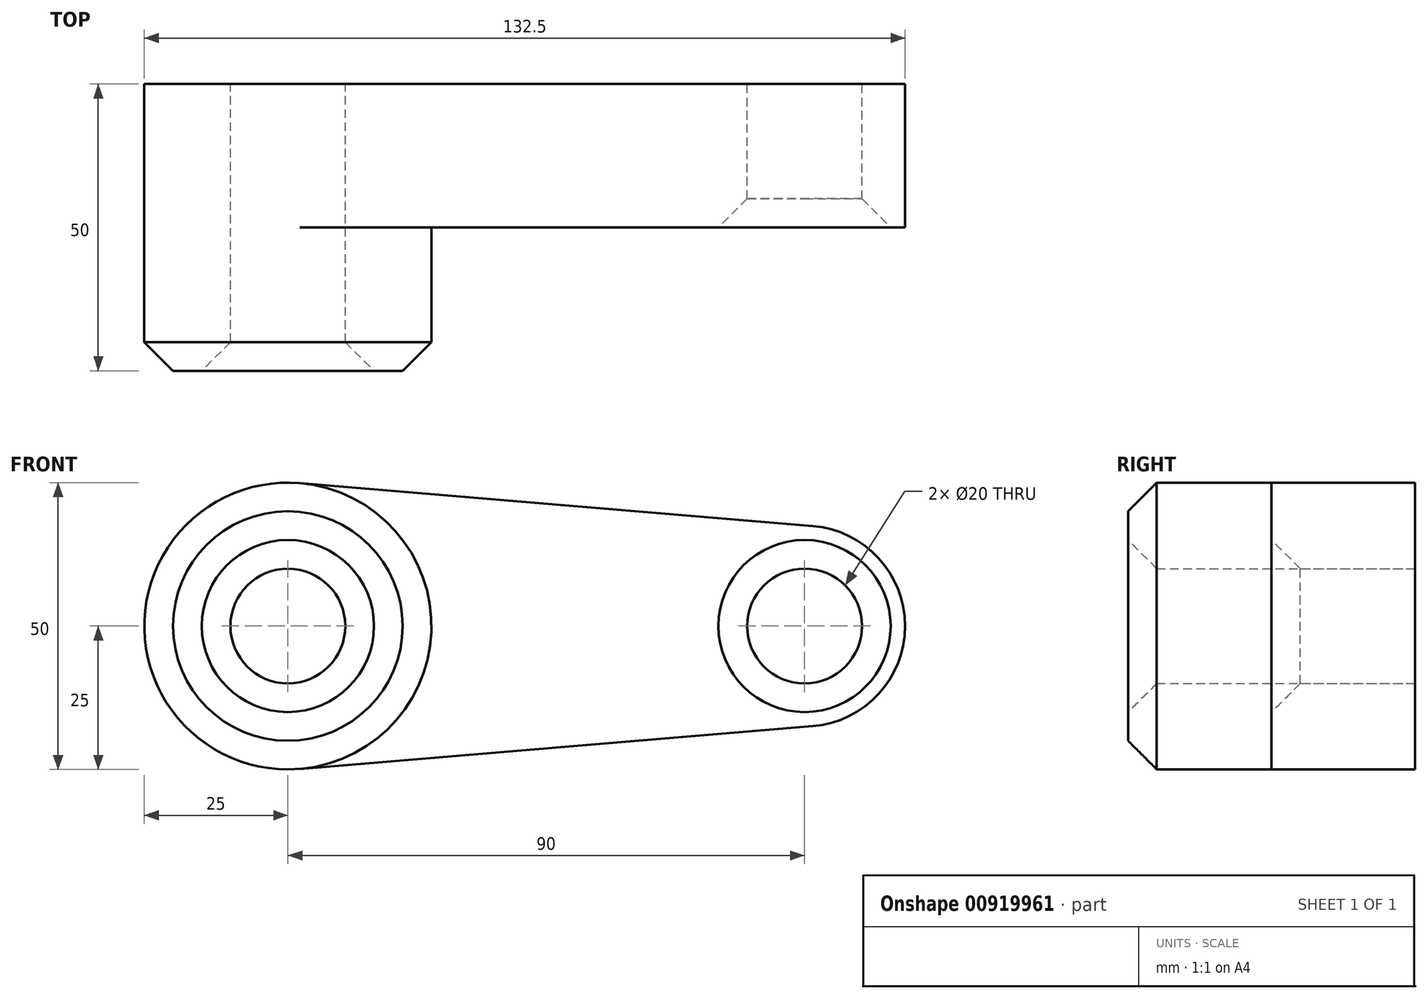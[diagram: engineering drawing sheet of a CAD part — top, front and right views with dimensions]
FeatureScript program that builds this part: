
annotation { "Feature Type Name" : "Feature", "Feature Type Description" : "" }
export const myFeature = defineFeature(function(context is Context, id is Id, definition is map)
    precondition{}
    {
        {
            var Q0;
            Q0=qCreatedBy(makeId("Front.planeOp"),FACE);
            var sketch = newSketch(context, id + "F0", { "sketchPlane" : qUnion([Q0])});
            skCircle(sketch, "E0", {"center": v(0, 0) * mm, "radius": 25 * mm});
            skCircle(sketch, "E1", {"center": v(90, 0) * mm, "radius": 17.5 * mm});
            skLineSegment(sketch, "E2", {"start": v(2.08, 24.91) * mm, "end": v(91.46, 17.44) * mm});
            skLineSegment(sketch, "E3", {"start": v(2.08, -24.91) * mm, "end": v(91.46, -17.44) * mm});
            skCircle(sketch, "E4", {"center": v(0, 0) * mm, "radius": 10 * mm});
            skCircle(sketch, "E5", {"center": v(90, 0) * mm, "radius": 10 * mm});
            skSolve(sketch);
        }
        {
            var Q0;
            {var subQ0=sQuery(id+"F0.wireOp",EDGE,"E2");Q0=makeQuery(id+"F0.imprint","IMPRINT",FACE,{"disambiguationData":[TD([[makeQuery(id+"F0.imprint","IMPRINT",EDGE,{"derivedFrom":subQ0}),-1.0]])]});}
            var Q1;
            Q1=makeQuery(id+"F0.imprint","IMPRINT",FACE,{"disambiguationData":[TD([[makeQuery(id+"F0.imprint","IMPRINT",EDGE,{"derivedFrom":sQuery(id+"F0.wireOp",EDGE,"E5")}),-1.0]])]});
            var Q2;
            Q2=makeQuery(id+"F0.imprint","IMPRINT",FACE,{"disambiguationData":[TD([[makeQuery(id+"F0.imprint","IMPRINT",EDGE,{"derivedFrom":sQuery(id+"F0.wireOp",EDGE,"E4")}),-1.0]])]});
            extrude(context, id + "F1", {"entities" : qUnion([Q0, Q1, Q2]), "depth" : 25 * mm, "offsetDistance" : 25 * mm});
        }
        {
            var Q0;
            Q0=makeQuery(id+"F0.imprint","IMPRINT",FACE,{"disambiguationData":[TD([[makeQuery(id+"F0.imprint","IMPRINT",EDGE,{"derivedFrom":sQuery(id+"F0.wireOp",EDGE,"E4")}),-1.0]])]});
            extrude(context, id + "F2", {"entities" : qUnion([Q0]), "operationType" : NewBodyOperationType.ADD, "depth" : 50 * mm, "offsetDistance" : 25 * mm});
        }
        {
            var Q0;
            Q0=makeQuery(id+"F2.opExtrude","CAP_EDGE",EDGE,{"disambiguationData":[OSD([sQuery(id+"F0.wireOp",EDGE,"E0")])],"isStart":false});
            var Q1;
            Q1=makeQuery(id+"F2.opExtrude","CAP_EDGE",EDGE,{"disambiguationData":[OSD([sQuery(id+"F0.wireOp",EDGE,"E4")])],"isStart":false});
            var Q2;
            Q2=makeQuery(id+"F1.opExtrude","CAP_EDGE",EDGE,{"disambiguationData":[OSD([sQuery(id+"F0.wireOp",EDGE,"E5")])],"isStart":false});
            chamfer(context, id + "F3", {"entities" : qUnion([Q0, Q1, Q2]), "width" : 5 * mm, "tangentPropagation" : true});
        }
    });
